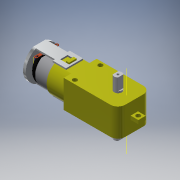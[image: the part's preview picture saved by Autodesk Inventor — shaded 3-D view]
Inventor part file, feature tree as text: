
AUTODESK INVENTOR PART (.ipt)
format: ipt  version: 2019 (Build 230136000, 136)  size: 562,688 bytes
history: native  units: mm
features: sketch x25, extrude x23, plane x5, projected_geometry x4, direct_edit x2, other x2, hole x1, revolve x1
ambient origin geometry x8: Origin, YZ Plane, XZ Plane, XY Plane, X Axis, Y Axis, Z Axis, Center Point
bodies: Solid1 (feature_tree)
feature tree (63):
  extrude  "Extrusion1"  Depth=11.0mm
  hole  "Hole1"  [1 undecoded]
  plane  "Work Plane1"
  extrude  "Extrusion2"  Depth=17.2mm
  extrude  "Extrusion3"  TaperAngle=0.0deg  [1 undecoded]
  extrude  "Extrusion4"  Depth=5.0mm
  revolve  "Revolution1"  [1 undecoded]
  extrude  "Extrusion5"  Depth=1.2mm
  extrude  "Extrusion6"  Depth=10.0mm
  extrude  "Extrusion7"  Depth=4.5mm
  extrude  "Extrusion8"  Depth=5.0mm
  plane  "Work Plane2"
  extrude  "Extrusion13"  Depth=1.0mm
  plane  "Work Plane3"
  extrude  "Extrusion14"  Depth=2.0mm TaperAngle=0.0deg
  extrude  "Extrusion15"  [1 undecoded]
  extrude  "Extrusion16"  Depth=4.5mm
  extrude  "Extrusion17"  [1 undecoded]
  extrude  "Extrusion18"  Depth=1.2mm
  extrude  "Extrusion19"  Depth=2.0mm
  extrude  "Extrusion20"  Depth=0.5mm
  plane  "Work Plane4"
  extrude  "Extrusion22"  Depth=0.5mm
  extrude  "Extrusion23"  Depth=0.5mm
  extrude  "Extrusion24"  Depth=0.5mm
  sketch  "Sketch27"  dims[d71=0.5mm d72=0.5mm]
  extrude  "Extrusion25"  Depth=1.0mm
  extrude  "Extrusion26"  Depth=0.2mm TaperAngle=0.0deg
  extrude  "Extrusion27"  Depth=10.0mm TaperAngle=0.0deg
  sketch  "Sketch31"  dims[d79=1.5mm d80=0.2mm d81=0.0mm]
  plane  "Work Plane5"
  extrude  "Extrusion29"  Depth=10.0mm
  direct_edit  "Direct Edit1"
  direct_edit  "Direct Edit2"
  sketch  "Sketch1"  dims[d0=36.5mm d1=11.0mm]
  sketch  "Sketch2"  dims[d2=22.25mm d3=5.0mm]
  sketch  "Sketch4"  dims[d4=18.75mm d5=0.0mm d6=17.2mm]
  sketch  "Sketch5"  dims[d7=5.0mm]
  sketch  "Sketch6"  dims[d8=3.0mm d9=6.0mm d10=4.0mm d11=2.0mm d12=90.0deg d13=8.0mm d14=20.594885mm d15=0.0mm]
  projected_geometry  "Projected Loop1"
  sketch  "Sketch7"  dims[d16=5.2mm d17=5.0mm]
  sketch  "Sketch8"  dims[d18=3.0mm d19=2.5mm d20=0.0mm]
  sketch  "Sketch9"  dims[d21=11.5mm d22=0.0mm d23=1.2mm]
  sketch  "Sketch10"  dims[d24=14.0mm d25=0.0mm d26=10.0mm]
  sketch  "Sketch11"  dims[d27=90.0deg d28=4.5mm]
  sketch  "Sketch16"  dims[d29=6.5mm d30=5.0mm]
  sketch  "Sketch17"  dims[d31=2.0mm d32=0.0mm d33=1.0mm]
  sketch  "Sketch18"  dims[d34=2.0mm d35=0.0mm d36=2.0mm d37=0.0mm]
  sketch  "Sketch19"  dims[d38=2.5mm d39=0.0mm d56=-0.1mm]
  sketch  "Sketch20"  dims[d57=0.2mm d58=0.0mm d59=4.5mm]
  sketch  "Sketch21"  dims[d60=15.0mm d61=-0.1mm]
  sketch  "Sketch22"  dims[d62=0.2mm d63=0.0mm d66=1.2mm]
  projected_geometry  "Projected Loop2"
  sketch  "Sketch23"  dims[d67=16.0mm d68=2.0mm]
  projected_geometry  "Projected Loop3"
  sketch  "Sketch26"  dims[d69=0.5mm d70=0.5mm]
  sketch  "Sketch28"  dims[d73=0.5mm d74=0.5mm]
  sketch  "Sketch29"  dims[d75=0.5mm d76=0.5mm]
  sketch  "Sketch30"  dims[d77=0.5mm d78=1.0mm]
  projected_geometry  "Projected Loop7"
  sketch  "Sketch32"  dims[d82=5.2mm d83=1.2mm d84=0.0mm d85=3.65mm d86=1.5mm d87=8.0mm d88=0.0mm d89=1.2mm d90=0.0mm d91=8.0mm d92=0.0mm d93=0.8mm d94=0.0mm d95=0.0mm d106=7.0mm d107=0.0mm d108=8.5mm d109=2.0mm d110=0.0mm d111=2.0mm d112=1.0mm d113=0.0mm d114=11.5mm d115=8.5mm d116=9.0mm d117=1.2mm d118=4.0mm d119=10.0mm d120=0.0mm d121=10.0mm d122=0.0mm d123=10.0mm d124=0.0mm d127=-2.0mm d128=1.9mm d129=0.0mm d130=9.0mm d131=10.0mm d132=10.0mm d133=9.0mm d134=10.0mm d135=10.0mm]
  other  "Scale1"
  other  "Scale2"
note: 5 required parameter values undecoded (feature->parameter linkage not recoverable at this tier; creation-order binding heuristic only, values carry confidence <= 0.55)